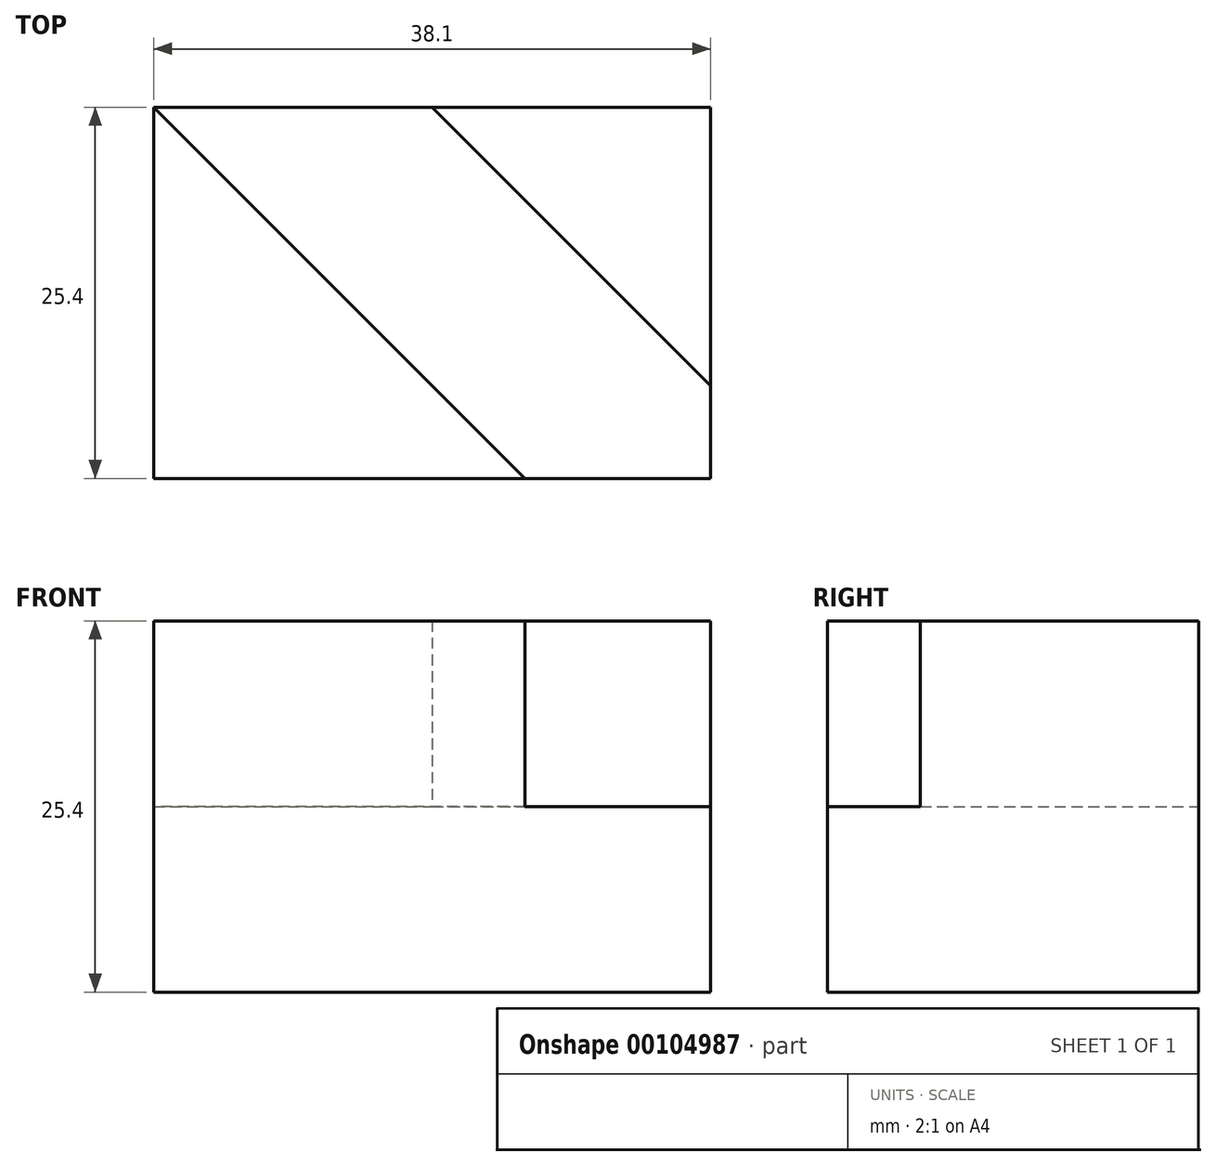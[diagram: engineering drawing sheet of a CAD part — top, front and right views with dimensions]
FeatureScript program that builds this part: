
annotation { "Feature Type Name" : "Feature", "Feature Type Description" : "" }
export const myFeature = defineFeature(function(context is Context, id is Id, definition is map)
    precondition{}
    {
        {
            var Q0;
            Q0=qCreatedBy(makeId("Front.planeOp"),FACE);
            var sketch = newSketch(context, id + "F0", { "sketchPlane" : qUnion([Q0])});
            skLineSegment(sketch, "E0.bottom", {"start": v(0, 0) * mm, "end": v(38.1, 0) * mm});
            skLineSegment(sketch, "E0.top", {"start": v(0, 25.4) * mm, "end": v(38.1, 25.4) * mm});
            skLineSegment(sketch, "E0.left", {"start": v(0, 0) * mm, "end": v(0, 25.4) * mm});
            skLineSegment(sketch, "E0.right", {"start": v(38.1, 0) * mm, "end": v(38.1, 25.4) * mm});
            skSolve(sketch);
        }
        {
            var Q0;
            Q0=qCreatedBy(makeId("Top.planeOp"),FACE);
            var sketch = newSketch(context, id + "F1", { "sketchPlane" : qUnion([Q0])});
            skLineSegment(sketch, "E1.bottom", {"start": v(25.4, 0) * mm, "end": v(38.1, 0) * mm});
            skLineSegment(sketch, "E1.top", {"start": v(0, 25.4) * mm, "end": v(19.05, 25.4) * mm});
            skLineSegment(sketch, "E1.right", {"start": v(38.1, 0) * mm, "end": v(38.1, 6.35) * mm});
            skLineSegment(sketch, "E2", {"start": v(0, 25.4) * mm, "end": v(25.4, 0) * mm});
            skLineSegment(sketch, "E3", {"start": v(38.1, 6.35) * mm, "end": v(19.05, 25.4) * mm});
            skPoint(sketch, "E4.orphan", {"position": v(0, 0) * mm});
            skPoint(sketch, "E5.orphan", {"position": v(38.1, 25.4) * mm});
            skSolve(sketch);
        }
        {
            var Q0;
            Q0 = qSketchRegion(id + "F0", true);
            extrude(context, id + "F2", {"entities" : qUnion([Q0]), "oppositeDirection" : true, "depth" : 25.4 * mm});
        }
        {
            var Q0;
            Q0 = qSketchRegion(id + "F1", true);
            extrude(context, id + "F3", {"entities" : qUnion([Q0]), "operationType" : NewBodyOperationType.REMOVE, "depth" : 25.4 * mm});
        }
        {
            var Q0;
            Q0=qCreatedBy(makeId("Front.planeOp"),FACE);
            var sketch = newSketch(context, id + "F4", { "sketchPlane" : qUnion([Q0])});
            skLineSegment(sketch, "E6.bottom", {"start": v(0, 0) * mm, "end": v(38.1, 0) * mm});
            skLineSegment(sketch, "E6.top", {"start": v(0, 12.7) * mm, "end": v(38.1, 12.7) * mm});
            skLineSegment(sketch, "E6.left", {"start": v(0, 0) * mm, "end": v(0, 12.7) * mm});
            skLineSegment(sketch, "E6.right", {"start": v(38.1, 0) * mm, "end": v(38.1, 12.7) * mm});
            skSolve(sketch);
        }
        {
            var Q0;
            Q0 = qSketchRegion(id + "F4", true);
            extrude(context, id + "F5", {"entities" : qUnion([Q0]), "operationType" : NewBodyOperationType.ADD, "oppositeDirection" : true, "depth" : 25.4 * mm});
        }
    });
